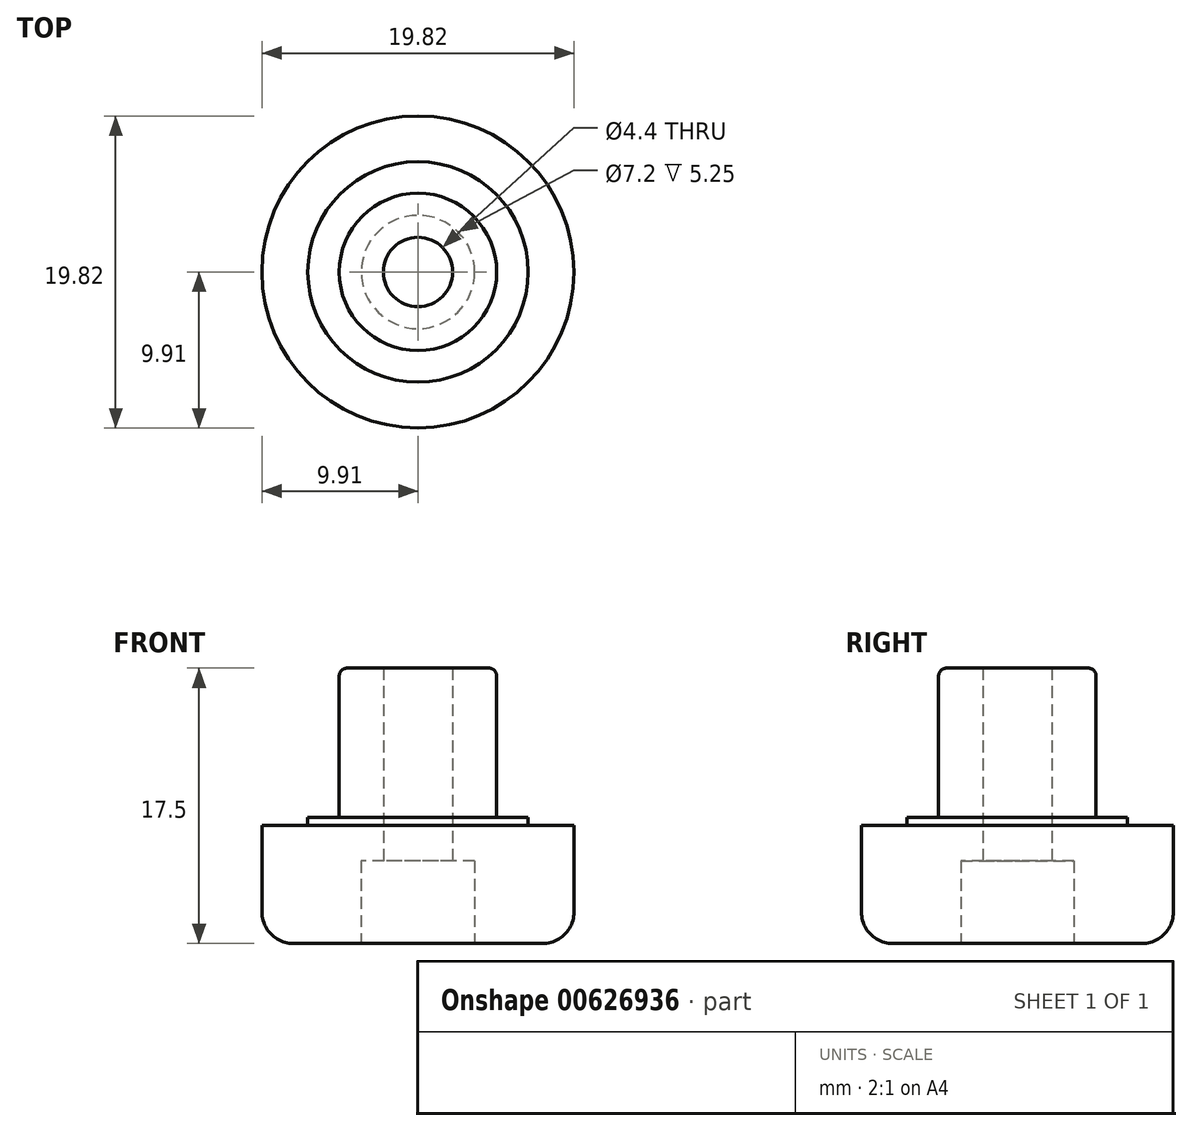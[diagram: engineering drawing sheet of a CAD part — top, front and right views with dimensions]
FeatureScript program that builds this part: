
annotation { "Feature Type Name" : "Feature", "Feature Type Description" : "" }
export const myFeature = defineFeature(function(context is Context, id is Id, definition is map)
    precondition{}
    {
        {
            var Q0;
            Q0=qCreatedBy(makeId("Top.planeOp"),FACE);
            var sketch = newSketch(context, id + "F0", { "sketchPlane" : qUnion([Q0])});
            skCircle(sketch, "E0", {"center": v(0, 0) * mm, "radius": 9.9 * mm});
            skCircle(sketch, "E1", {"center": v(0, 0) * mm, "radius": 5 * mm});
            skCircle(sketch, "E2", {"center": v(0, 0) * mm, "radius": 2.2 * mm});
            skCircle(sketch, "E3", {"center": v(0, 0) * mm, "radius": 3.6 * mm});
            skSolve(sketch);
        }
        {
            var Q0;
            Q0=makeQuery(id+"F0.imprint","IMPRINT",FACE,{"disambiguationData":[TD([[makeQuery(id+"F0.imprint","IMPRINT",EDGE,{"derivedFrom":sQuery(id+"F0.wireOp",EDGE,"E1")}),1.0]])]});
            var Q1;
            Q1=makeQuery(id+"F0.imprint","IMPRINT",FACE,{"disambiguationData":[TD([[makeQuery(id+"F0.imprint","IMPRINT",EDGE,{"derivedFrom":sQuery(id+"F0.wireOp",EDGE,"E2")}),-1.0]])]});
            extrude(context, id + "F1", {"entities" : qUnion([Q0, Q1]), "depth" : 17.5 * mm, "offsetDistance" : 25.4 * mm});
        }
        {
            var Q0;
            Q0=makeQuery(id+"F0.imprint","IMPRINT",FACE,{"disambiguationData":[TD([[makeQuery(id+"F0.imprint","IMPRINT",EDGE,{"derivedFrom":sQuery(id+"F0.wireOp",EDGE,"E0")}),1.0]])]});
            extrude(context, id + "F2", {"entities" : qUnion([Q0]), "operationType" : NewBodyOperationType.ADD, "depth" : 7.5 * mm, "offsetDistance" : 25.4 * mm});
        }
        {
            var Q0;
            Q0=makeQuery(id+"F0.imprint","IMPRINT",FACE,{"disambiguationData":[TD([[makeQuery(id+"F0.imprint","IMPRINT",EDGE,{"derivedFrom":sQuery(id+"F0.wireOp",EDGE,"E2")}),-1.0]])]});
            extrude(context, id + "F3", {"entities" : qUnion([Q0]), "operationType" : NewBodyOperationType.REMOVE, "depth" : 5.25 * mm, "offsetDistance" : 25 * mm});
        }
        {
            var Q0;
            Q0=makeQuery(id+"F2.opExtrude","CAP_EDGE",EDGE,{"disambiguationData":[OSD([sQuery(id+"F0.wireOp",EDGE,"E0")])],"isStart":true});
            fillet(context, id + "F4", {"entities" : qUnion([Q0]), "radius" : 2 * mm, "tangentPropagation" : true, "allowEdgeOverflow" : false});
        }
        {
            var Q0;
            Q0=makeQuery(id+"F1.opExtrude","CAP_EDGE",EDGE,{"disambiguationData":[OSD([sQuery(id+"F0.wireOp",EDGE,"E1")])],"isStart":false});
            fillet(context, id + "F5", {"entities" : qUnion([Q0]), "radius" : 0.5 * mm, "tangentPropagation" : true, "allowEdgeOverflow" : false});
        }
        {
            var Q0;
            Q0=makeQuery(id+"F2.opExtrude","CAP_FACE",FACE,{"disambiguationData":[OSD([sQuery(id+"F0.wireOp",EDGE,"E0"),sQuery(id+"F0.wireOp",EDGE,"E1")])],"isStart":false});
            var sketch = newSketch(context, id + "F6", { "sketchPlane" : qUnion([Q0])});
            skCircle(sketch, "E4", {"center": v(0, 0) * mm, "radius": 7 * mm});
            skSolve(sketch);
        }
        {
            var Q0;
            Q0=makeQuery(id+"F6.imprint","IMPRINT",FACE,{"disambiguationData":[TD([[makeQuery(id+"F6.imprint","IMPRINT",EDGE,{"derivedFrom":sQuery(id+"F6.wireOp",EDGE,"E4")}),1.0]])]});
            extrude(context, id + "F7", {"entities" : qUnion([Q0]), "operationType" : NewBodyOperationType.ADD, "depth" : 0.5 * mm, "offsetDistance" : 25 * mm});
        }
    });
